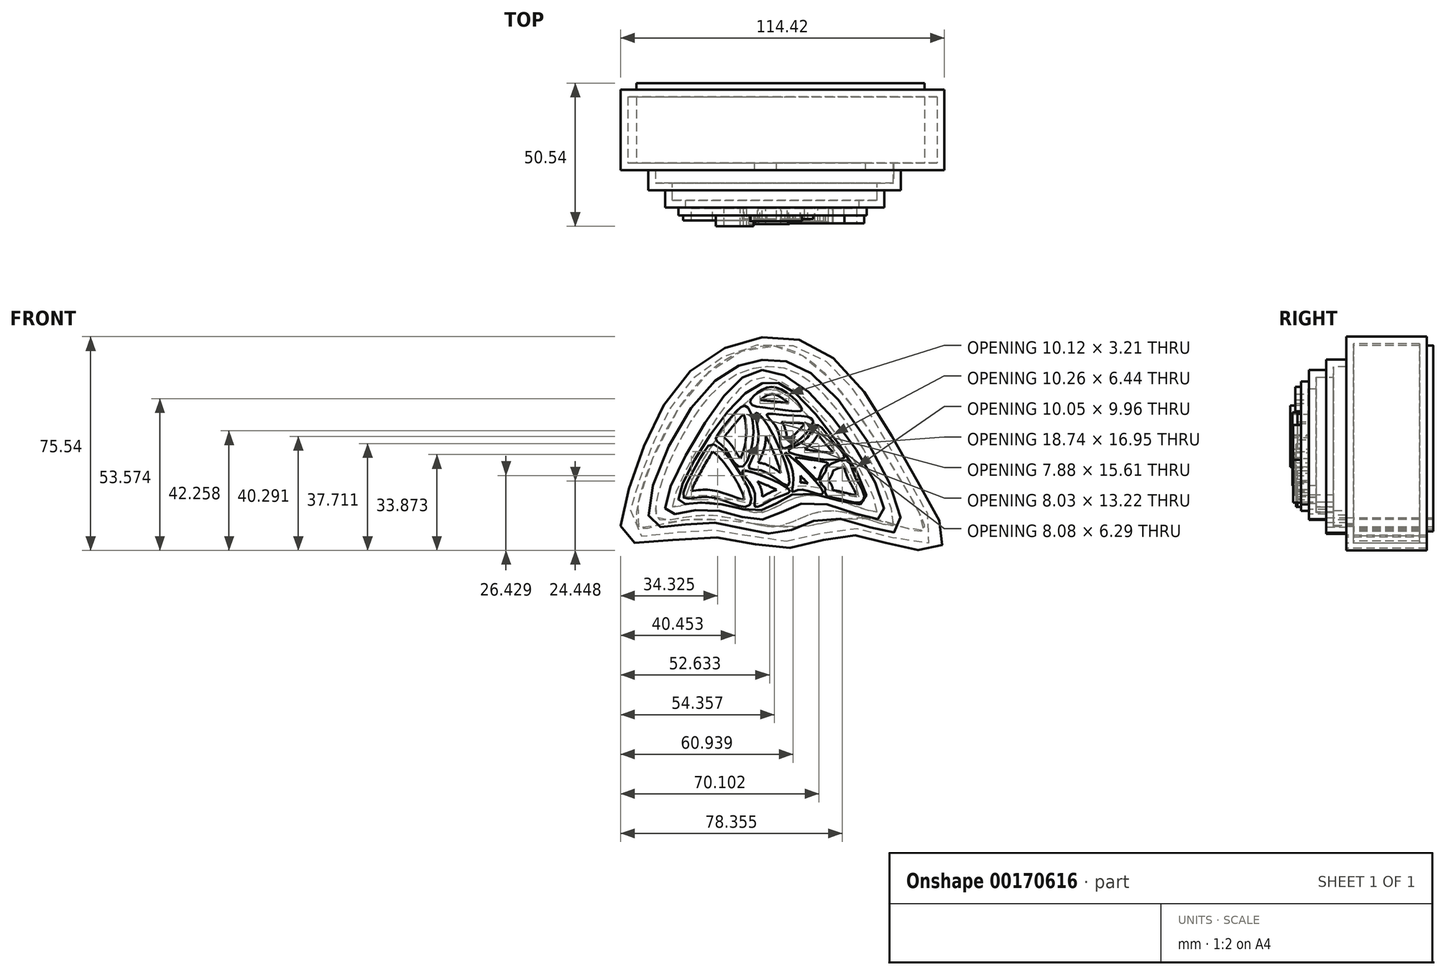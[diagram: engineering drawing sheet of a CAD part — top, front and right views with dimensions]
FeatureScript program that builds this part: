
annotation { "Feature Type Name" : "Feature", "Feature Type Description" : "" }
export const myFeature = defineFeature(function(context is Context, id is Id, definition is map)
    precondition{}
    {
        {
            var Q0;
            Q0=qCreatedBy(makeId("Front.planeOp"),FACE);
            var sketch = newSketch(context, id + "F0", { "sketchPlane" : qUnion([Q0])});
            skFitSpline(sketch, "E0", {"points": [v(0, 58.33) * mm, v(-28.1, 43.67) * mm, v(-46.11, 7.94) * mm, v(-48.25, -13.13) * mm, v(-19.54, -12.22) * mm, v(8.55, -16.19) * mm, v(30.54, -11.6) * mm, v(50.39, -16.19) * mm, v(63.82, -14.66) * mm, v(54.36, 8.25) * mm, v(26.26, 50.08) * mm, v(0, 58.33) * mm]});
            skSolve(sketch);
        }
        {
            var Q0;
            Q0 = qSketchRegion(id + "F0", true);
            extrude(context, id + "F1", {"entities" : qUnion([Q0]), "oppositeDirection" : true, "depth" : 28.45 * mm});
        }
        {
            var Q0;
            Q0=qCreatedBy(makeId("Front.planeOp"),FACE);
            var sketch = newSketch(context, id + "F2", { "sketchPlane" : qUnion([Q0])});
            skFitSpline(sketch, "E1", {"points": [v(0, 50.39) * mm, v(-23.2, 36.04) * mm, v(-39.4, -7.02) * mm, v(-19.85, -7.02) * mm, v(5.5, -11) * mm, v(25.35, -5.5) * mm, v(48.25, -9.77) * mm, v(24.13, 39.4) * mm, v(0, 50.39) * mm]});
            skSolve(sketch);
        }
        {
            var Q0;
            Q0 = qSketchRegion(id + "F2", true);
            extrude(context, id + "F3", {"entities" : qUnion([Q0]), "operationType" : NewBodyOperationType.ADD, "depth" : 7.11 * mm});
        }
        {
            var Q0;
            Q0=qCreatedBy(makeId("Front.planeOp"),FACE);
            var sketch = newSketch(context, id + "F4", { "sketchPlane" : qUnion([Q0])});
            skFitSpline(sketch, "E2", {"points": [v(0, 46.72) * mm, v(-19.85, 28.7) * mm, v(-33.9, -3.36) * mm, v(-19.85, -2.44) * mm, v(0, -6.1) * mm, v(17.71, 0) * mm, v(42.14, -5.5) * mm, v(27.79, 26.26) * mm, v(0, 46.72) * mm]});
            skSolve(sketch);
        }
        {
            var Q0;
            Q0 = qSketchRegion(id + "F4", true);
            extrude(context, id + "F5", {"entities" : qUnion([Q0]), "operationType" : NewBodyOperationType.ADD, "depth" : 13.2 * mm});
        }
        {
            var Q0;
            Q0=qCreatedBy(makeId("Front.planeOp"),FACE);
            var sketch = newSketch(context, id + "F6", { "sketchPlane" : qUnion([Q0])});
            skFitSpline(sketch, "E3", {"points": [v(0, 42.14) * mm, v(-20.77, 20.16) * mm, v(-29.32, 0) * mm, v(-19.54, 0) * mm, v(0, -2.75) * mm, v(13.74, 3.36) * mm, v(36.34, 0) * mm, v(15.88, 34.5) * mm, v(0, 42.14) * mm]});
            skSolve(sketch);
        }
        {
            var Q0;
            Q0 = qSketchRegion(id + "F6", true);
            extrude(context, id + "F7", {"entities" : qUnion([Q0]), "operationType" : NewBodyOperationType.ADD, "depth" : 16 * mm});
        }
        {
            var Q0;
            Q0=qCreatedBy(makeId("Front.planeOp"),FACE);
            var sketch = newSketch(context, id + "F8", { "sketchPlane" : qUnion([Q0])});
            skFitSpline(sketch, "E4", {"points": [v(-20.51, 18.01) * mm, v(-25.6, 8.92) * mm, v(-27.79, 1.65) * mm, v(-21.24, 1.9) * mm, v(-11.9, 0) * mm, v(-5.6, -1.5) * mm, v(-3.91, 1.65) * mm, v(-16.88, 20.44) * mm, v(-20.51, 18.01) * mm]});
            skSolve(sketch);
        }
        {
            var Q0;
            Q0 = qSketchRegion(id + "F8", true);
            extrude(context, id + "F9", {"entities" : qUnion([Q0]), "operationType" : NewBodyOperationType.ADD, "depth" : 17.78 * mm});
        }
        {
            var Q0;
            Q0=qCreatedBy(makeId("Front.planeOp"),FACE);
            var sketch = newSketch(context, id + "F10", { "sketchPlane" : qUnion([Q0])});
            skFitSpline(sketch, "E5", {"points": [v(-9.01, 32.33) * mm, v(-13.22, 27.46) * mm, v(-16.44, 22.25) * mm, v(-13.78, 19.7) * mm, v(-7.9, 12.5) * mm, v(-3.25, 22.58) * mm, v(-5.8, 34.1) * mm, v(-9.01, 32.33) * mm]});
            skSolve(sketch);
        }
        {
            var Q0;
            Q0 = qSketchRegion(id + "F10", true);
            extrude(context, id + "F11", {"entities" : qUnion([Q0]), "operationType" : NewBodyOperationType.ADD, "depth" : 19.8 * mm});
        }
        {
            var Q0;
            Q0=qCreatedBy(makeId("Front.planeOp"),FACE);
            var sketch = newSketch(context, id + "F12", { "sketchPlane" : qUnion([Q0])});
            skFitSpline(sketch, "E6", {"points": [v(-6.99, 11.13) * mm, v(-2.9, 4.15) * mm, v(-2.5, -1.52) * mm, v(5.53, 1.9) * mm, v(9.62, 4.41) * mm, v(-6.99, 11.13) * mm]});
            skSolve(sketch);
        }
        {
            var Q0;
            Q0 = qSketchRegion(id + "F12", true);
            extrude(context, id + "F13", {"entities" : qUnion([Q0]), "operationType" : NewBodyOperationType.ADD, "depth" : 17.27 * mm});
        }
        {
            var Q0;
            Q0=qCreatedBy(makeId("Front.planeOp"),FACE);
            var sketch = newSketch(context, id + "F14", { "sketchPlane" : qUnion([Q0])});
            skFitSpline(sketch, "E7", {"points": [v(-4.26, 35.16) * mm, v(0, 39.82) * mm, v(7.29, 39.64) * mm, v(14, 32.74) * mm, v(5.8, 32.93) * mm, v(-4.26, 35.16) * mm]});
            skSolve(sketch);
        }
        {
            var Q0;
            Q0 = qSketchRegion(id + "F14", true);
            extrude(context, id + "F15", {"entities" : qUnion([Q0]), "operationType" : NewBodyOperationType.ADD, "depth" : 18.03 * mm});
        }
        {
            var Q0;
            Q0=qCreatedBy(makeId("Front.planeOp"),FACE);
            var sketch = newSketch(context, id + "F16", { "sketchPlane" : qUnion([Q0])});
            skFitSpline(sketch, "E8", {"points": [v(-2.4, 31.62) * mm, v(-1.47, 21.19) * mm, v(-4.82, 12.24) * mm, v(0.66, 10.94) * mm, v(9.24, 6) * mm, v(3.18, 25.17) * mm, v(-2.4, 31.62) * mm]});
            skSolve(sketch);
        }
        {
            var Q0;
            Q0 = qSketchRegion(id + "F16", true);
            extrude(context, id + "F17", {"entities" : qUnion([Q0]), "operationType" : NewBodyOperationType.ADD, "depth" : 19.05 * mm});
        }
        {
            var Q0;
            Q0=qCreatedBy(makeId("Front.planeOp"),FACE);
            var sketch = newSketch(context, id + "F18", { "sketchPlane" : qUnion([Q0])});
            skFitSpline(sketch, "E9", {"points": [v(1.6, 30.92) * mm, v(5.48, 25.62) * mm, v(7.72, 19.1) * mm, v(17.91, 28.47) * mm, v(9.96, 30.72) * mm, v(1.6, 30.92) * mm]});
            skSolve(sketch);
        }
        {
            var Q0;
            Q0 = qSketchRegion(id + "F18", true);
            extrude(context, id + "F19", {"entities" : qUnion([Q0]), "operationType" : NewBodyOperationType.ADD, "depth" : 17.27 * mm});
        }
        {
            var Q0;
            Q0=qCreatedBy(makeId("Front.planeOp"),FACE);
            var sketch = newSketch(context, id + "F20", { "sketchPlane" : qUnion([Q0])});
            skFitSpline(sketch, "E10", {"points": [v(8.03, 17.63) * mm, v(10.73, 11.15) * mm, v(10.67, 3.7) * mm, v(13.2, 4.46) * mm, v(20.98, 2.84) * mm, v(21.1, 4.51) * mm, v(8.03, 17.63) * mm]});
            skSolve(sketch);
        }
        {
            var Q0;
            Q0 = qSketchRegion(id + "F20", true);
            extrude(context, id + "F21", {"entities" : qUnion([Q0]), "operationType" : NewBodyOperationType.ADD, "depth" : 18.03 * mm});
        }
        {
            var Q0;
            Q0=qCreatedBy(makeId("Front.planeOp"),FACE);
            var sketch = newSketch(context, id + "F22", { "sketchPlane" : qUnion([Q0])});
            skFitSpline(sketch, "E11", {"points": [v(9.17, 18.27) * mm, v(14.66, 21.72) * mm, v(18.52, 26.8) * mm, v(19.83, 27.26) * mm, v(24.87, 21.58) * mm, v(28.96, 15.77) * mm, v(15.48, 16.1) * mm, v(9.17, 18.27) * mm]});
            skSolve(sketch);
        }
        {
            var Q0;
            Q0 = qSketchRegion(id + "F22", true);
            extrude(context, id + "F23", {"entities" : qUnion([Q0]), "operationType" : NewBodyOperationType.ADD, "depth" : 18.8 * mm});
        }
        {
            var Q0;
            Q0=qCreatedBy(makeId("Front.planeOp"),FACE);
            var sketch = newSketch(context, id + "F24", { "sketchPlane" : qUnion([Q0])});
            skFitSpline(sketch, "E12", {"points": [v(11.67, 15.63) * mm, v(15.27, 11.98) * mm, v(19.08, 8.17) * mm, v(20.03, 8.43) * mm, v(21.53, 12.41) * mm, v(23.24, 13.83) * mm, v(15.83, 15.28) * mm, v(11.67, 15.63) * mm]});
            skSolve(sketch);
        }
        {
            var Q0;
            Q0 = qSketchRegion(id + "F24", true);
            extrude(context, id + "F25", {"entities" : qUnion([Q0]), "operationType" : NewBodyOperationType.ADD, "depth" : 18.29 * mm});
        }
        {
            var Q0;
            Q0=makeQuery(id+"F23.opExtrude","CAP_FACE",FACE,{"disambiguationData":[OSD([sQuery(id+"F22.wireOp",EDGE,"E11")])],"isStart":false});
            var sketch = newSketch(context, id + "F26", { "sketchPlane" : qUnion([Q0])});
            skFitSpline(sketch, "E13", {"points": [v(29.72, 14.87) * mm, v(32.1, 10.75) * mm, v(35.02, 4.96) * mm, v(35.83, 0.72) * mm, v(32.76, 0) * mm, v(26.73, 1.4) * mm, v(22.28, 2.82) * mm, v(22.24, 4.96) * mm, v(20.26, 7.23) * mm, v(22.24, 10.63) * mm, v(22.93, 12.65) * mm, v(29.72, 14.87) * mm]});
            skSolve(sketch);
        }
        {
            var Q0;
            Q0 = qSketchRegion(id + "F26", true);
            extrude(context, id + "F27", {"entities" : qUnion([Q0]), "operationType" : NewBodyOperationType.ADD, "oppositeDirection" : true, "depth" : 11.68 * mm});
        }
        {
            var Q0;
            Q0=makeQuery(id+"F17.opExtrude","CAP_FACE",FACE,{"disambiguationData":[OSD([sQuery(id+"F16.wireOp",EDGE,"E8")])],"isStart":false});
            var Q1;
            Q1=makeQuery(id+"F19.opExtrude","CAP_FACE",FACE,{"disambiguationData":[OSD([sQuery(id+"F18.wireOp",EDGE,"E9")])],"isStart":false});
            var Q2;
            Q2=makeQuery(id+"F15.opExtrude","CAP_FACE",FACE,{"disambiguationData":[OSD([sQuery(id+"F14.wireOp",EDGE,"E7")])],"isStart":false});
            var Q3;
            Q3=makeQuery(id+"F11.opExtrude","CAP_FACE",FACE,{"disambiguationData":[OSD([sQuery(id+"F10.wireOp",EDGE,"E5")])],"isStart":false});
            var Q4;
            Q4=makeQuery(id+"F9.opExtrude","CAP_FACE",FACE,{"disambiguationData":[OSD([sQuery(id+"F8.wireOp",EDGE,"E4")])],"isStart":false});
            var Q5;
            Q5=makeQuery(id+"F13.opExtrude","CAP_FACE",FACE,{"disambiguationData":[OSD([sQuery(id+"F12.wireOp",EDGE,"E6")])],"isStart":false});
            var Q6;
            Q6=makeQuery(id+"F21.opExtrude","CAP_FACE",FACE,{"disambiguationData":[OSD([sQuery(id+"F20.wireOp",EDGE,"E10")])],"isStart":false});
            var Q7;
            Q7=makeQuery(id+"F23.opExtrude","CAP_FACE",FACE,{"disambiguationData":[OSD([sQuery(id+"F22.wireOp",EDGE,"E11")])],"isStart":false});
            var Q8;
            Q8=makeQuery(id+"F27.opExtrude","CAP_FACE",FACE,{"disambiguationData":[OSD([sQuery(id+"F26.wireOp",EDGE,"E13")])],"isStart":true});
            var Q9;
            Q9=makeQuery(id+"F25.opExtrude","CAP_FACE",FACE,{"disambiguationData":[OSD([sQuery(id+"F24.wireOp",EDGE,"E12")])],"isStart":false});
            shell(context, id + "F28", {"entities" : qUnion([Q0, Q1, Q2, Q3, Q4, Q5, Q6, Q7, Q8, Q9]), "thickness" : 2.54 * mm});
        }
        {
            var Q0;
            Q0=qCreatedBy(makeId("Front.planeOp"),FACE);
            var sketch = newSketch(context, id + "F29", { "sketchPlane" : qUnion([Q0])});
            skFitSpline(sketch, "E14", {"points": [v(4.28, 55.27) * mm, v(26.26, 40.92) * mm, v(51.91, 2.75) * mm, v(56.8, -10.08) * mm, v(38.48, -5.8) * mm, v(14.66, -8.55) * mm, v(-7.02, -7.02) * mm, v(-34.2, -7.33) * mm, v(-43.97, -8.55) * mm, v(-26.57, 37.56) * mm, v(4.28, 55.27) * mm]});
            skSolve(sketch);
        }
        {
            var Q0;
            Q0 = qSketchRegion(id + "F29", true);
            extrude(context, id + "F30", {"entities" : qUnion([Q0]), "operationType" : NewBodyOperationType.ADD, "oppositeDirection" : true, "depth" : 30.73 * mm});
        }
    });
